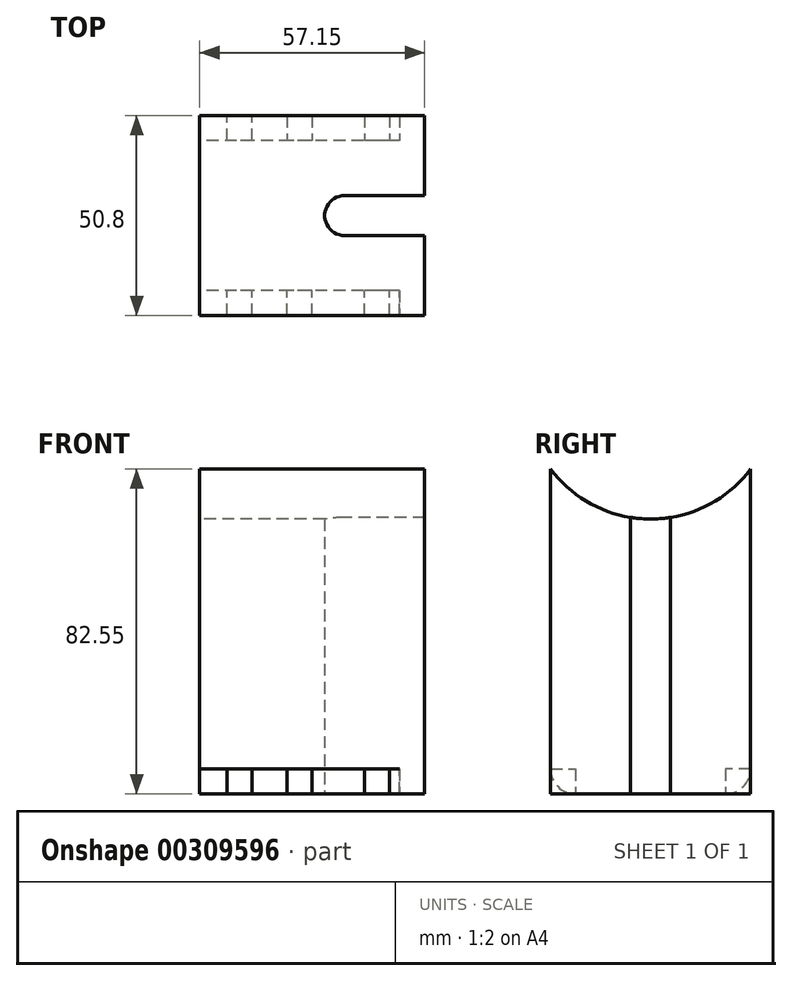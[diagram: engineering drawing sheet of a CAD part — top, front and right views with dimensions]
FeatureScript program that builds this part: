
annotation { "Feature Type Name" : "Feature", "Feature Type Description" : "" }
export const myFeature = defineFeature(function(context is Context, id is Id, definition is map)
    precondition{}
    {
        {
            var Q0;
            Q0=qCreatedBy(makeId("Right.planeOp"),FACE);
            var sketch = newSketch(context, id + "F0", { "sketchPlane" : qUnion([Q0])});
            skLineSegment(sketch, "E0.top", {"start": v(-36.03, -38.1) * mm, "end": v(14.77, -38.1) * mm});
            skLineSegment(sketch, "E0.left", {"start": v(-36.03, 44.46) * mm, "end": v(-36.03, -38.1) * mm});
            skLineSegment(sketch, "E0.right", {"start": v(14.77, 44.46) * mm, "end": v(14.77, -38.1) * mm});
            skArc(sketch, "E1", {"start": v(-36.03, 44.46) * mm, "mid": v(-10.63, 31.76) * mm, "end": v(14.77, 44.46) * mm});
            skSolve(sketch);
        }
        {
            var Q0;
            Q0=makeQuery(id+"F0.imprint","IMPRINT",FACE,{"disambiguationData":[TD([[makeQuery(id+"F0.imprint","IMPRINT",EDGE,{"derivedFrom":sQuery(id+"F0.wireOp",EDGE,"E0.top")}),1.0]])]});
            extrude(context, id + "F1", {"entities" : qUnion([Q0]), "depth" : 57.15 * mm});
        }
        {
            var Q0;
            Q0=makeQuery(id+"F1.opExtrude","CAP_FACE",FACE,{"disambiguationData":[OSD([sQuery(id+"F0.wireOp",EDGE,"E0.top"),sQuery(id+"F0.wireOp",EDGE,"E0.left"),sQuery(id+"F0.wireOp",EDGE,"E0.right"),sQuery(id+"F0.wireOp",EDGE,"E1")])],"isStart":true});
            var sketch = newSketch(context, id + "F2", { "sketchPlane" : qUnion([Q0])});
            skSolve(sketch);
        }
        {
            var Q0;
            Q0=makeQuery(id+"F1.opExtrude","SWEPT_FACE",FACE,{"disambiguationData":[OSD([sQuery(id+"F0.wireOp",EDGE,"E0.top")])]});
            var sketch = newSketch(context, id + "F3", { "sketchPlane" : qUnion([Q0])});
            skLineSegment(sketch, "E2", {"start": v(57.15, 15.7) * mm, "end": v(36.83, 15.7) * mm});
            skLineSegment(sketch, "E3", {"start": v(36.83, 5.55) * mm, "end": v(57.15, 5.55) * mm});
            skLineSegment(sketch, "E4", {"start": v(57.15, 15.7) * mm, "end": v(57.15, 5.55) * mm});
            skArc(sketch, "E5", {"start": v(36.83, 15.7) * mm, "mid": v(31.75, 10.63) * mm, "end": v(36.83, 5.55) * mm});
            skSolve(sketch);
        }
        {
            var Q0;
            Q0=makeQuery(id+"F3.imprint","IMPRINT",FACE,{"disambiguationData":[TD([[makeQuery(id+"F3.imprint","IMPRINT",EDGE,{"derivedFrom":sQuery(id+"F3.wireOp",EDGE,"E2")}),1.0]])]});
            extrude(context, id + "F4", {"entities" : qUnion([Q0]), "operationType" : NewBodyOperationType.REMOVE, "oppositeDirection" : true, "depth" : 101.6 * mm});
        }
        {
            var Q0;
            Q0=makeQuery(id+"F1.opExtrude","SWEPT_FACE",FACE,{"disambiguationData":[OSD([sQuery(id+"F0.wireOp",EDGE,"E0.top")])]});
            var sketch = newSketch(context, id + "F5", { "sketchPlane" : qUnion([Q0])});
            skLineSegment(sketch, "E6.bottom", {"start": v(48.26, 36.03) * mm, "end": v(41.91, 36.03) * mm});
            skLineSegment(sketch, "E6.top", {"start": v(48.26, 29.68) * mm, "end": v(41.91, 29.68) * mm});
            skLineSegment(sketch, "E6.left", {"start": v(48.26, 36.03) * mm, "end": v(48.26, 29.68) * mm});
            skLineSegment(sketch, "E6.right", {"start": v(41.91, 36.03) * mm, "end": v(41.91, 29.68) * mm});
            skLineSegment(sketch, "E7.bottom", {"start": v(48.26, -14.77) * mm, "end": v(41.91, -14.77) * mm});
            skLineSegment(sketch, "E7.top", {"start": v(48.26, -8.42) * mm, "end": v(41.91, -8.42) * mm});
            skLineSegment(sketch, "E7.left", {"start": v(48.26, -14.77) * mm, "end": v(48.26, -8.42) * mm});
            skLineSegment(sketch, "E7.right", {"start": v(41.91, -14.77) * mm, "end": v(41.91, -8.42) * mm});
            skLineSegment(sketch, "E8.bottom", {"start": v(28.58, 36.03) * mm, "end": v(22.23, 36.03) * mm});
            skLineSegment(sketch, "E8.top", {"start": v(28.58, 29.68) * mm, "end": v(22.23, 29.68) * mm});
            skLineSegment(sketch, "E8.left", {"start": v(28.58, 36.03) * mm, "end": v(28.58, 29.68) * mm});
            skLineSegment(sketch, "E8.right", {"start": v(22.23, 36.03) * mm, "end": v(22.23, 29.68) * mm});
            skLineSegment(sketch, "E9.bottom", {"start": v(28.58, -14.77) * mm, "end": v(22.23, -14.77) * mm});
            skLineSegment(sketch, "E9.top", {"start": v(28.58, -8.42) * mm, "end": v(22.23, -8.42) * mm});
            skLineSegment(sketch, "E9.left", {"start": v(28.58, -14.77) * mm, "end": v(28.58, -8.42) * mm});
            skLineSegment(sketch, "E9.right", {"start": v(22.23, -14.77) * mm, "end": v(22.23, -8.42) * mm});
            skLineSegment(sketch, "E10.bottom", {"start": v(13.34, 36.03) * mm, "end": v(6.99, 36.03) * mm});
            skLineSegment(sketch, "E10.top", {"start": v(13.34, 29.68) * mm, "end": v(6.99, 29.68) * mm});
            skLineSegment(sketch, "E10.left", {"start": v(13.34, 36.03) * mm, "end": v(13.34, 29.68) * mm});
            skLineSegment(sketch, "E10.right", {"start": v(6.99, 36.03) * mm, "end": v(6.99, 29.68) * mm});
            skLineSegment(sketch, "E11.bottom", {"start": v(13.34, -8.42) * mm, "end": v(6.99, -8.42) * mm});
            skLineSegment(sketch, "E11.top", {"start": v(13.34, -14.77) * mm, "end": v(6.99, -14.77) * mm});
            skLineSegment(sketch, "E11.left", {"start": v(13.34, -8.42) * mm, "end": v(13.34, -14.77) * mm});
            skLineSegment(sketch, "E11.right", {"start": v(6.99, -8.42) * mm, "end": v(6.99, -14.77) * mm});
            skSolve(sketch);
        }
        {
            var Q0;
            Q0=makeQuery(id+"F5.imprint","IMPRINT",FACE,{"disambiguationData":[TD([[makeQuery(id+"F5.imprint","IMPRINT",EDGE,{"derivedFrom":sQuery(id+"F5.wireOp",EDGE,"E6.bottom")}),1.0]])]});
            var Q1;
            Q1=makeQuery(id+"F5.imprint","IMPRINT",FACE,{"disambiguationData":[TD([[makeQuery(id+"F5.imprint","IMPRINT",EDGE,{"derivedFrom":sQuery(id+"F5.wireOp",EDGE,"E8.bottom")}),1.0]])]});
            var Q2;
            Q2=makeQuery(id+"F5.imprint","IMPRINT",FACE,{"disambiguationData":[TD([[makeQuery(id+"F5.imprint","IMPRINT",EDGE,{"derivedFrom":sQuery(id+"F5.wireOp",EDGE,"E9.bottom")}),-1.0]])]});
            var Q3;
            Q3=makeQuery(id+"F5.imprint","IMPRINT",FACE,{"disambiguationData":[TD([[makeQuery(id+"F5.imprint","IMPRINT",EDGE,{"derivedFrom":sQuery(id+"F5.wireOp",EDGE,"E7.bottom")}),-1.0]])]});
            var Q4;
            Q4=makeQuery(id+"F5.imprint","IMPRINT",FACE,{"disambiguationData":[TD([[makeQuery(id+"F5.imprint","IMPRINT",EDGE,{"derivedFrom":sQuery(id+"F5.wireOp",EDGE,"E10.bottom")}),1.0]])]});
            var Q5;
            Q5=makeQuery(id+"F5.imprint","IMPRINT",FACE,{"disambiguationData":[TD([[makeQuery(id+"F5.imprint","IMPRINT",EDGE,{"derivedFrom":sQuery(id+"F5.wireOp",EDGE,"E11.bottom")}),1.0]])]});
            extrude(context, id + "F6", {"entities" : qUnion([Q0, Q1, Q2, Q3, Q4, Q5]), "operationType" : NewBodyOperationType.REMOVE, "oppositeDirection" : true, "depth" : 6.35 * mm});
        }
        {
            var Q0;
            Q0=makeQuery(id+"F2.imprint","IMPRINT",FACE,{"disambiguationData":[TD([[makeQuery(id+"F2.imprint","IMPRINT",EDGE,{"derivedFrom":makeQuery(id+"F1.opExtrude","CAP_EDGE",EDGE,{"disambiguationData":[OSD([sQuery(id+"F0.wireOp",EDGE,"E0.top")])],"isStart":true})}),-1.0]])]});
            var sketch = newSketch(context, id + "F7", { "sketchPlane" : qUnion([Q0])});
            skLineSegment(sketch, "E12", {"start": v(36.03, -31.74) * mm, "end": v(29.68, -31.74) * mm});
            skLineSegment(sketch, "E13", {"start": v(29.68, -31.74) * mm, "end": v(29.68, -38.1) * mm});
            skArc(sketch, "E14", {"start": v(29.68, -38.1) * mm, "mid": v(34.17, -36.23) * mm, "end": v(36.03, -31.74) * mm});
            skLineSegment(sketch, "E15", {"start": v(-14.77, -31.74) * mm, "end": v(-8.42, -31.74) * mm});
            skLineSegment(sketch, "E16", {"start": v(-8.42, -31.74) * mm, "end": v(-8.42, -38.1) * mm});
            skArc(sketch, "E17", {"start": v(-14.77, -31.74) * mm, "mid": v(-12.91, -36.23) * mm, "end": v(-8.42, -38.1) * mm});
            skSolve(sketch);
        }
        {
            var Q0;
            Q0 = qSketchRegion(id + "F7", true);
            extrude(context, id + "F8", {"entities" : qUnion([Q0]), "oppositeDirection" : true, "depth" : 50.8 * mm});
        }
    });
